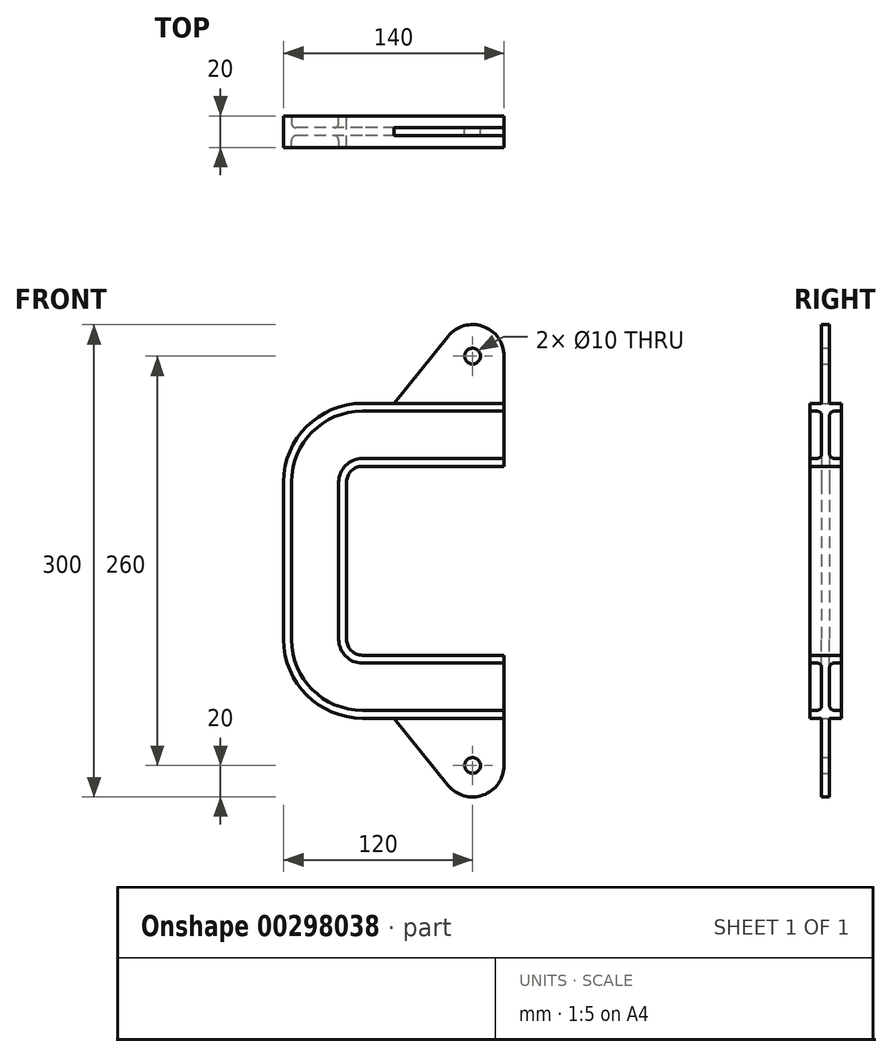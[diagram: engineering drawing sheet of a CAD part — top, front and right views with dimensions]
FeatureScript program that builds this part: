
annotation { "Feature Type Name" : "Feature", "Feature Type Description" : "" }
export const myFeature = defineFeature(function(context is Context, id is Id, definition is map)
    precondition{}
    {
        {
            var Q0;
            Q0=qCreatedBy(makeId("Front.planeOp"),FACE);
            var sketch = newSketch(context, id + "F0", { "sketchPlane" : qUnion([Q0])});
            skLineSegment(sketch, "E0", {"start": v(0, 60) * mm, "end": v(-90, 60) * mm});
            skLineSegment(sketch, "E1", {"start": v(-100, 50) * mm, "end": v(-100, 0) * mm});
            skPoint(sketch, "E2.visualSharp", {"position": v(-100, 60) * mm});
            skArc(sketch, "E2.filletArc", {"start": v(-90, 60) * mm, "mid": v(-97.07, 57.07) * mm, "end": v(-100, 50) * mm});
            skSolve(sketch);
        }
        {
            var Q0;
            Q0=qCreatedBy(makeId("Right.planeOp"),FACE);
            var sketch = newSketch(context, id + "F1", { "sketchPlane" : qUnion([Q0])});
            skLineSegment(sketch, "E3", {"start": v(0, 100) * mm, "end": v(10, 100) * mm});
            skLineSegment(sketch, "E4", {"start": v(10, 100) * mm, "end": v(10, 95) * mm});
            skLineSegment(sketch, "E5", {"start": v(10, 95) * mm, "end": v(5.5, 95) * mm});
            skLineSegment(sketch, "E6", {"start": v(2.5, 92) * mm, "end": v(2.5, 68) * mm});
            skLineSegment(sketch, "E7", {"start": v(5.5, 65) * mm, "end": v(10, 65) * mm});
            skLineSegment(sketch, "E8", {"start": v(10, 65) * mm, "end": v(10, 60) * mm});
            skLineSegment(sketch, "E9", {"start": v(10, 60) * mm, "end": v(0, 60) * mm});
            skLineSegment(sketch, "E10.MirrorCS", {"start": v(-10, 100) * mm, "end": v(-10, 95) * mm});
            skLineSegment(sketch, "E11.MirrorCS", {"start": v(-10, 65) * mm, "end": v(-10, 60) * mm});
            skLineSegment(sketch, "E12.MirrorCS", {"start": v(0, 100) * mm, "end": v(-10, 100) * mm});
            skLineSegment(sketch, "E13.MirrorCS", {"start": v(-5.5, 65) * mm, "end": v(-10, 65) * mm});
            skLineSegment(sketch, "E14.MirrorCS", {"start": v(-10, 95) * mm, "end": v(-5.5, 95) * mm});
            skLineSegment(sketch, "E15.MirrorCS", {"start": v(-10, 60) * mm, "end": v(0, 60) * mm});
            skLineSegment(sketch, "E16.MirrorCS", {"start": v(-2.5, 92) * mm, "end": v(-2.5, 68) * mm});
            skPoint(sketch, "E17.visualSharp", {"position": v(-2.5, 95) * mm});
            skArc(sketch, "E17.filletArc", {"start": v(-2.5, 92) * mm, "mid": v(-3.38, 94.12) * mm, "end": v(-5.5, 95) * mm});
            skPoint(sketch, "E18.visualSharp", {"position": v(2.5, 95) * mm});
            skArc(sketch, "E18.filletArc", {"start": v(5.5, 95) * mm, "mid": v(3.38, 94.12) * mm, "end": v(2.5, 92) * mm});
            skPoint(sketch, "E19.visualSharp", {"position": v(2.5, 65) * mm});
            skArc(sketch, "E19.filletArc", {"start": v(2.5, 68) * mm, "mid": v(3.38, 65.88) * mm, "end": v(5.5, 65) * mm});
            skPoint(sketch, "E20.visualSharp", {"position": v(-2.5, 65) * mm});
            skArc(sketch, "E20.filletArc", {"start": v(-5.5, 65) * mm, "mid": v(-3.38, 65.88) * mm, "end": v(-2.5, 68) * mm});
            skSolve(sketch);
        }
        {
            var Q0;
            Q0=makeQuery(id+"F1.imprint","IMPRINT",FACE,{"disambiguationData":[TD([[makeQuery(id+"F1.imprint","IMPRINT",EDGE,{"derivedFrom":sQuery(id+"F1.wireOp",EDGE,"E3")}),-1.0]])]});
            var Q1;
            Q1=sQuery(id+"F0.wireOp",EDGE,"E0");
            var Q2;
            Q2=sQuery(id+"F0.wireOp",EDGE,"E2.filletArc");
            var Q3;
            Q3=sQuery(id+"F0.wireOp",EDGE,"E1");
            sweep(context, id + "F2", {"profiles" : qUnion([Q0]), "path" : qUnion([Q1, Q2, Q3])});
        }
        {
            var Q0;
            Q0=makeQuery(id+"F2.opSweep","SWEPT_BODY",BODY,{"disambiguationData":[OSD([sQuery(id+"F0.wireOp",EDGE,"E1"),sQuery(id+"F1.wireOp",EDGE,"E3"),sQuery(id+"F1.wireOp",EDGE,"E4"),sQuery(id+"F1.wireOp",EDGE,"E5"),sQuery(id+"F1.wireOp",EDGE,"E6"),sQuery(id+"F1.wireOp",EDGE,"E7"),sQuery(id+"F1.wireOp",EDGE,"E8"),sQuery(id+"F1.wireOp",EDGE,"E9"),sQuery(id+"F1.wireOp",EDGE,"E10.MirrorCS"),sQuery(id+"F1.wireOp",EDGE,"E11.MirrorCS"),sQuery(id+"F1.wireOp",EDGE,"E12.MirrorCS"),sQuery(id+"F1.wireOp",EDGE,"E13.MirrorCS"),sQuery(id+"F1.wireOp",EDGE,"E14.MirrorCS"),sQuery(id+"F1.wireOp",EDGE,"E15.MirrorCS"),sQuery(id+"F1.wireOp",EDGE,"E16.MirrorCS"),sQuery(id+"F1.wireOp",EDGE,"E17.filletArc"),sQuery(id+"F1.wireOp",EDGE,"E18.filletArc"),sQuery(id+"F1.wireOp",EDGE,"E19.filletArc"),sQuery(id+"F1.wireOp",EDGE,"E20.filletArc")])]});
            var Q1;
            Q1=qCreatedBy(makeId("Top.planeOp"),FACE);
            mirror(context, id + "F3", {"operationType" : NewBodyOperationType.ADD, "entities" : qUnion([Q0]), "mirrorPlane" : qUnion([Q1])});
        }
        {
            var Q0;
            Q0=qCreatedBy(makeId("Front.planeOp"),FACE);
            var sketch = newSketch(context, id + "F4", { "sketchPlane" : qUnion([Q0])});
            skLineSegment(sketch, "E21", {"start": v(0, -100) * mm, "end": v(0, -130) * mm});
            skLineSegment(sketch, "E22", {"start": v(-35.55, -142.58) * mm, "end": v(-70, -100) * mm});
            skLineSegment(sketch, "E23", {"start": v(-70, -100) * mm, "end": v(0, -100) * mm});
            skPoint(sketch, "E24.visualSharp", {"position": v(0, -186.51) * mm});
            skArc(sketch, "E24.filletArc", {"start": v(-35.55, -142.58) * mm, "mid": v(-13.33, -148.85) * mm, "end": v(0, -130) * mm});
            skCircle(sketch, "E25", {"center": v(-20, -130) * mm, "radius": 5 * mm});
            skSolve(sketch);
        }
        {
            var Q0;
            Q0 = qSketchRegion(id + "F4", true);
            extrude(context, id + "F5", {"entities" : qUnion([Q0]), "operationType" : NewBodyOperationType.ADD, "endBound" : BoundingType.SYMMETRIC, "depth" : 5 * mm});
        }
        {
            var Q0;
            Q0=makeQuery(id+"F2.opSweep","SWEPT_BODY",BODY,{"disambiguationData":[OSD([sQuery(id+"F0.wireOp",EDGE,"E1"),sQuery(id+"F1.wireOp",EDGE,"E3"),sQuery(id+"F1.wireOp",EDGE,"E4"),sQuery(id+"F1.wireOp",EDGE,"E5"),sQuery(id+"F1.wireOp",EDGE,"E6"),sQuery(id+"F1.wireOp",EDGE,"E7"),sQuery(id+"F1.wireOp",EDGE,"E8"),sQuery(id+"F1.wireOp",EDGE,"E9"),sQuery(id+"F1.wireOp",EDGE,"E10.MirrorCS"),sQuery(id+"F1.wireOp",EDGE,"E11.MirrorCS"),sQuery(id+"F1.wireOp",EDGE,"E12.MirrorCS"),sQuery(id+"F1.wireOp",EDGE,"E13.MirrorCS"),sQuery(id+"F1.wireOp",EDGE,"E14.MirrorCS"),sQuery(id+"F1.wireOp",EDGE,"E15.MirrorCS"),sQuery(id+"F1.wireOp",EDGE,"E16.MirrorCS"),sQuery(id+"F1.wireOp",EDGE,"E17.filletArc"),sQuery(id+"F1.wireOp",EDGE,"E18.filletArc"),sQuery(id+"F1.wireOp",EDGE,"E19.filletArc"),sQuery(id+"F1.wireOp",EDGE,"E20.filletArc")])]});
            var Q1;
            Q1=qCreatedBy(makeId("Top.planeOp"),FACE);
            mirror(context, id + "F6", {"operationType" : NewBodyOperationType.ADD, "entities" : qUnion([Q0]), "mirrorPlane" : qUnion([Q1])});
        }
    });
